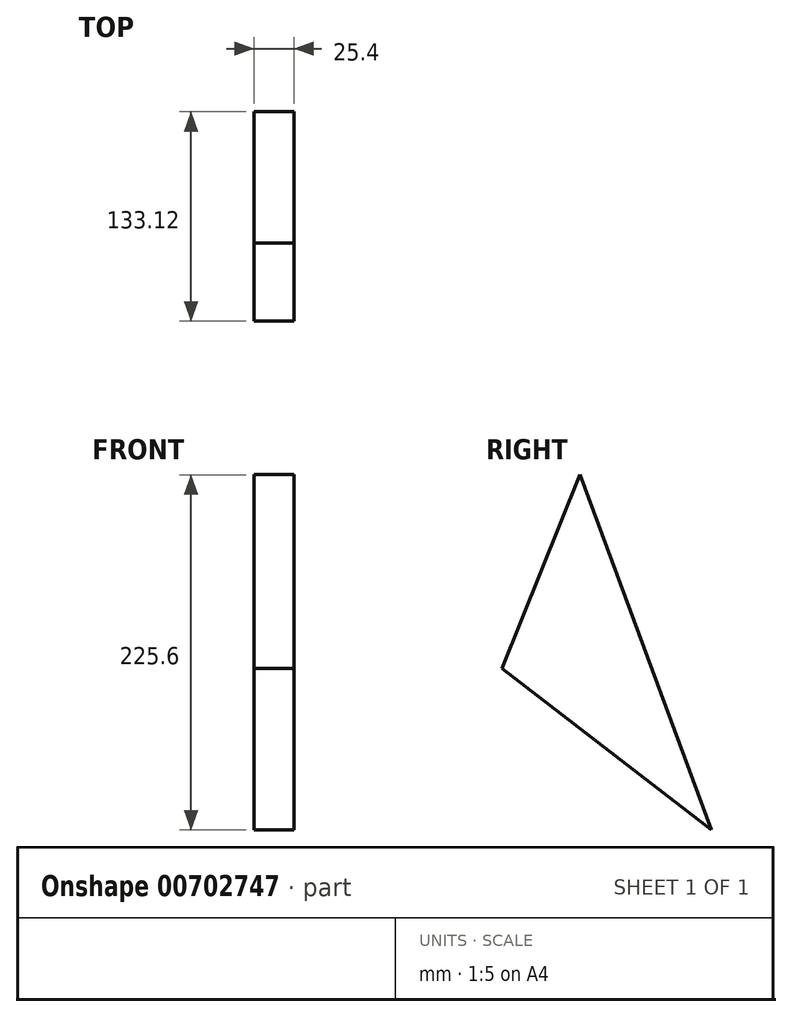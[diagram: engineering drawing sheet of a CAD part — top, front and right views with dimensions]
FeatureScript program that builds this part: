
annotation { "Feature Type Name" : "Feature", "Feature Type Description" : "" }
export const myFeature = defineFeature(function(context is Context, id is Id, definition is map)
    precondition{}
    {
        {
            var Q0;
            Q0=qCreatedBy(makeId("Right.planeOp"),FACE);
            var sketch = newSketch(context, id + "F0", { "sketchPlane" : qUnion([Q0])});
            skLineSegment(sketch, "E0", {"start": v(-59.34, 44.87) * mm, "end": v(73.78, -57.7) * mm});
            skLineSegment(sketch, "E1", {"start": v(73.78, -57.7) * mm, "end": v(-9.74, 167.9) * mm});
            skLineSegment(sketch, "E2", {"start": v(-9.74, 167.9) * mm, "end": v(-59.34, 44.87) * mm});
            skSolve(sketch);
        }
        {
            var Q0;
            Q0=makeQuery(id+"F0.imprint","IMPRINT",FACE,{"disambiguationData":[TD([[makeQuery(id+"F0.imprint","IMPRINT",EDGE,{"derivedFrom":sQuery(id+"F0.wireOp",EDGE,"E0")}),1.0]])]});
            extrude(context, id + "F1", {"entities" : qUnion([Q0]), "depth" : 25.4 * mm, "offsetDistance" : 25.4 * mm});
        }
    });
